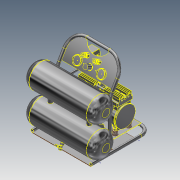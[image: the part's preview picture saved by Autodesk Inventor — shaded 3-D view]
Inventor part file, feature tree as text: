
AUTODESK INVENTOR PART (.ipt)
format: ipt  version: 2020.3 (Build 243373000, 373)  size: 10,528,256 bytes
history: native  units: in
note: dims shown in document units (in); Inventor stores cm internally (conversion verified against a paired STEP export)
features: other x64, surface_op x53, sketch x3, plane x1, extrude x1
ambient origin geometry x8: Origin, YZ Plane, XZ Plane, XY Plane, X Axis, Y Axis, Z Axis, Center Point
bodies: Solid1 (feature_tree), Solid2 (feature_tree), Solid3 (feature_tree), Solid4 (feature_tree), Solid5 (feature_tree), Solid6 (feature_tree), Solid7 (feature_tree)
feature tree (122):
  sketch  "Sketch1"  dims[d0=0.38in d1=-0.375in]
  plane  "Work Plane1"
  sketch  "Sketch2"  dims[d2=12.0in]
  other  "Work Axis1"
  other  "Work Axis2"
  other  "Work Axis3"
  other  "Work Axis4"
  extrude  "Extrusion1"  [1 undecoded]
  sketch  "Sketch3"  dims[d3=11.0in d4=9.75in d5=2.6in d6=0.1in d7=0.0in d8=0.23in d9=0.23in d10=0.23in]
  parser-record x1  (decoder bookkeeping rows leaked as tree rows — omitted from the tree; the rows remain in map.json)
  other  "NONE:1"
  other  "NONE:2"
  other  "NONE:3"
  other  "NONE:4"
  other  "NONE:5"
  other  "NONE:6"
  surface_op  "Surface1"
  surface_op  "Surface2"
  surface_op  "Surface3"
  surface_op  "Surface4"
  surface_op  "Surface5"
  surface_op  "Surface6"
  surface_op  "Surface7"
  surface_op  "Surface8"
  surface_op  "Surface9"
  surface_op  "Surface10"
  surface_op  "Surface11"
  surface_op  "Surface12"
  surface_op  "Surface13"
  surface_op  "Surface14"
  surface_op  "Surface15"
  surface_op  "Surface16"
  surface_op  "Surface17"
  surface_op  "Surface18"
  surface_op  "Surface19"
  surface_op  "Surface20"
  surface_op  "Surface21"
  surface_op  "Surface22"
  surface_op  "Surface23"
  surface_op  "Surface24"
  surface_op  "Surface25"
  surface_op  "Surface26"
  surface_op  "Surface27"
  surface_op  "Surface28"
  surface_op  "Surface29"
  surface_op  "Surface30"
  surface_op  "Surface31"
  surface_op  "Surface32"
  surface_op  "Surface33"
  surface_op  "Surface34"
  surface_op  "Surface35"
  surface_op  "Surface40"
  surface_op  "Surface41"
  surface_op  "Surface42"
  surface_op  "Surface43"
  surface_op  "Surface44"
  surface_op  "Surface45"
  surface_op  "Surface46"
  surface_op  "Surface47"
  surface_op  "Surface48"
  surface_op  "Surface49"
  surface_op  "Surface50"
  surface_op  "Surface51"
  surface_op  "Surface52"
  surface_op  "Surface53"
  surface_op  "Surface54"
  surface_op  "Surface55"
  surface_op  "Surface56"
  surface_op  "Surface57"
  other  "Srf2"
  other  "Srf3"
  other  "Srf4"
  other  "Srf5"
  other  "Srf6"
  other  "Srf7"
  other  "Srf8"
  other  "Srf9"
  other  "Srf10"
  other  "Srf11"
  other  "Srf12"
  other  "Srf13"
  other  "Srf14"
  other  "Srf15"
  other  "Srf16"
  other  "Srf17"
  other  "Srf18"
  other  "Srf19"
  other  "Srf20"
  other  "Srf21"
  other  "Srf22"
  other  "Srf23"
  other  "Srf24"
  other  "Srf25"
  other  "Srf26"
  other  "Srf27"
  other  "Srf28"
  other  "Srf29"
  other  "Srf30"
  other  "Srf31"
  other  "Srf32"
  other  "Srf33"
  other  "Srf34"
  other  "Srf35"
  other  "Srf36"
  other  "Srf41"
  other  "Srf42"
  other  "Srf43"
  other  "Srf44"
  other  "Srf45"
  other  "Srf46"
  other  "Srf47"
  other  "Srf48"
  other  "Srf49"
  other  "Srf50"
  other  "Srf51"
  other  "Srf52"
  other  "Srf53"
  other  "Srf54"
  other  "Srf55"
  other  "Srf56"
  other  "Srf57"
  other  "Srf58"
note: 1 required parameter value undecoded (feature->parameter linkage not recoverable at this tier; creation-order binding heuristic only, values carry confidence <= 0.55)
